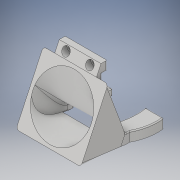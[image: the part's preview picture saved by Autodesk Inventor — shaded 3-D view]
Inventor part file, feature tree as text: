
AUTODESK INVENTOR PART (.ipt)
format: ipt  version: 2019.4 (Build 234330000, 330)  size: 1,016,832 bytes
history: native  units: mm
features: other x26, fillet x14, extrude x8, loft x3, projected_geometry x2
ambient origin geometry x8: Origin, YZ Plane, XZ Plane, XY Plane, X Axis, Y Axis, Z Axis, Center Point
bodies: Solid1 (feature_tree)
feature tree (53):
  other  "Bottom Shaft Plane"
  extrude  "Bottom Shaft"  Depth=6.4mm TaperAngle=0.0deg
  other  "Vent Cutout Sketch"
  other  "Angled Fan House Starting Plane"
  other  "Outer Horizontal Boundary Plane"
  other  "Angle Reference Sketch"
  other  "Fan Sketch"
  other  "Angled Rectangle Starting Plane"
  other  "Angled Rectangle Plane (-.6)"
  loft  "Fan Top Loft"
  loft  "Fan Bottom Loft"
  other  "Angled Rectangle"
  other  "Bottom Vent Cutaway Plane"
  loft  "Fan Loft cut"
  extrude  "Vent Cutout Extrusion (5.4)"  TaperAngle=90.0deg  [1 undecoded]
  fillet  "Inner Vent Round Fillet (3.25)"  [1 undecoded]
  other  "Starting Bottom Vent Cutaway Plane"
  extrude  "Bottom Vent Cutaway Extrusion (To)"  TaperAngle=90.0deg  [1 undecoded]
  fillet  "Inner Vent Grove Fillet (2)"  [1 undecoded]
  fillet  "Opening Vent Fillet (.7)"  [1 undecoded]
  fillet  "Opening Vent Fillet (.4)"  Radius=2.6mm
  fillet  "Loft to Vent Face Fillet (2.7)"  Radius=2.6mm
  fillet  "Top Vent Fillet (.65)"  Radius=1.6mm
  fillet  "Bottom Base Vent Fillet (.4)"  Radius=1.6mm
  fillet  "Bottom Vent Fillet (.36)"  Radius=1.6mm
  fillet  "Right Loft Support Fillet (.44)"  Radius=1.6mm
  fillet  "Left Loft Support Fillet (.44)"  [1 undecoded]
  other  "Starting Support Plane"
  extrude  "Support Extrusion (28)"  Depth=11.34464mm
  other  "Support Counterbore Starting Plane"
  extrude  "Support Counterbore Extrusion (To Next)"  Depth=6.8mm
  other  "Support Hole Starting Plane"
  extrude  "Support Small Hole (Through)"  TaperAngle=0.0deg  [1 undecoded]
  extrude  "Vent Bottom Backside Cutaway Extrusion (Through)"  TaperAngle=0.0deg  [1 undecoded]
  fillet  "Vent Round Fillet (.4)"  [1 undecoded]
  extrude  "Vent Cut"  TaperAngle=0.0deg  [1 undecoded]
  fillet  "Bottom Vent Fillet (.95)"  [1 undecoded]
  fillet  "Support Trim Fillet (.4)"  Radius=5.4mm
  fillet  "Supprt Trim Fillet (.8)"  [1 undecoded]
  other  "Bottom Shaft Sketch"
  other  "Angled Rectangle Loft Sketch"
  other  "Edges5"
  other  "Edges6"
  other  "Bottom Rectangle"
  other  "Circle"
  other  "Bottom Vent Cutaway Sketch"
  other  "Support Counterbore Sketch (5.2)"
  other  "Support Small Holes Sketch (2.8)"
  other  "Vent Bottom Backside Cutaway Sketch"
  other  "Inner Vent Cut Sketch"
  projected_geometry  "Projected Loop4"
  projected_geometry  "Projected Loop5"
  other  "Support Sketch"
note: 12 required parameter values undecoded (feature->parameter linkage not recoverable at this tier; creation-order binding heuristic only, values carry confidence <= 0.55)
